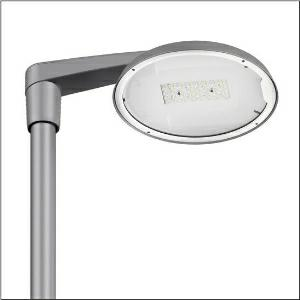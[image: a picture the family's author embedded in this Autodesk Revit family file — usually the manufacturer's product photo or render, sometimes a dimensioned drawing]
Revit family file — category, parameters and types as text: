
# Revit family: dl_r__50_iq_mini___st0_5a_5xa248b31f08ge_dbc8
name_source: partatom
category: Lighting Fixtures
units: mm (PartAtom-declared; Revit-internal decimal feet)

## family parameters
Cut with Voids When Loaded = No
Host = Face
Light Source = No
Part Type = Normal
Room Calculation Point = No
Round Connector Dimension = Use Diameter
Shared = No

## types (1)
- --- (1 x LED, 5190 lm, 32.7 W, 3000K)
    Apparent Load = 33 VA
    CIE Flux Codes = 41 75 97 100 100
    Color Rendering = 70
    Color Temperature = 3000K
    Default Elevation = 1800 mm
    Description = DL® 50 iQ mini, mast luminaire, primary light control with lens, of PMMA, primary optical cover: cover, of toughened safety glass, transparent, light distribution: ST0.5a, light emission: direct distribution, primary light characteristic: asymmetric, installation type: side-entry, post-top, LED, High Power LED, rated luminous flux: 5.190lm, luminous efficacy: 159lm/W, light colour: 730, colour temperature: 3000K, control gear: iQ Street-Remote, control: optimised constant luminous flux control (CLO 2.0), Desk-Remote (wireless, voltage-free reading and setting of iQ features in the workshop via application-optimized NFC function/RFID function), Light-Fading, Smart-Wire, Night-Set, Lumen-Switch, Temp-Guard, Auto-Match, Street-Remote, mains connection: 230..240V, AC, 50/60Hz, connection cable pre-assembled, cable length: 6,5m, start of lifetime: 33W, end of service life: 34W, reduction: 16W, luminaire housing, of diecast aluminium, powder-coated, Siteco® metallic grey (DB 702S), inclination adjustable: 0°, 5°, 10° (post-top) | 0°, -5°, -10°, -15° (side-entry), please order mast post-top element or mast side-entry element separately, diameter: 500mm, height: 115mm, post-top: for spigot size d x l = 76 x 100mm; with reducer (optional accessory) 60 x 100mm | side-entry: for spigot size d x l = 60 x 100mm; with reducer (optional accessory) 42 x 100mm, mounting height: 4..6m, protection rating (complete): IP66, insulation class (complete): insulation class II (safety insulation), certification: CE, ENEC, ENEC+, VDE, impact resistance: IK08, permissible operating ambient temperature for outdoor applications: -25..+40°C, standard-compliant lighting for roads and squares, packaging unit: 1 piece

Light Distribution: ST0.5a
    Height = 115 mm
    Lamp = 1 x LED
    Lamp Light Flux = 5190 lm
    Lamp Power = 32.7 W
    Lamp count = 1
    Length = 500 mm
    Luminous efficacy = 159 lm/W
    Manufacturer = Siteco
    ModVariant = No
    Model = 5XA248B31F08GE
    Number of Poles = 1
    OnlyDefault = Yes
    Power Factor = 1
    Product Name = DL® 50 iQ mini | ST0.5a
    Product group = mast luminaire | pylon top
    ProductGroupID = 6100
    Protection Class = Protection class II
    Protection Degree = IP 66
    RLX_Detail_Level = 1
    RLX_Emergency_Light_Flux = 0 lm
    RLX_Emergency_Type = 0
    RLX_Emergency_Type_DB = No
    RlxData = <blob elided: 127101 chars, md5=f9d0bc84>
    Socket = socket
    Standby Power = 0 W
    System Light Flux = 5190 lm
    System Power = 33 W
    Type Comments = factory setting: luminous flux: 100 % | dim-lin: 254 | 340 mA
    Type Image = l_1251794.jpg
    URL = http://relux.com
    VarID = @adj_164779
    Voltage = 0 V
    Weight = 0.00 kg
    Width = 0 mm  [stored 0 ft]

note: [stored X ft] marks values corroborated as IEEE doubles in the binary element streams (Revit-internal decimal feet)

## geometry (parser evidence)
native form markers: Blend x4, Sweep x12
no freeform markers — native parametric forms only
